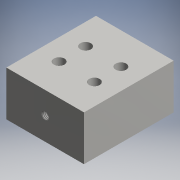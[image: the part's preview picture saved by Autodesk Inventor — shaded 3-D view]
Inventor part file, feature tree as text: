
AUTODESK INVENTOR PART (.ipt)
format: ipt  version: 2016 (Build 200138000, 138)  size: 129,536 bytes
history: native  units: mm (DEFAULTED — no unit token found)
features: sketch x4, extrude x2, hole x2
ambient origin geometry x8: Origin, YZ Plane, XZ Plane, XY Plane, X Axis, Y Axis, Z Axis, Center Point
bodies: Solid1 (feature_tree)
feature tree (8):
  extrude  "Extrusion1"  Depth=44.0mm
  hole  "Hole1"  [1 undecoded]
  extrude  "Extrusion2"  Depth=5.0mm
  sketch  "Sketch2"  dims[d0=50.8mm d1=44.0mm]
  sketch  "Sketch3"  dims[d2=25.4mm d3=0.0mm]
  hole  "Hole2"  [1 undecoded]
  sketch  "Sketch5"  dims[d11=6.0mm d12=6.0mm d13=6.0mm d14=6.0mm d15=20.0mm d16=15.0mm d18=0.0mm d19=5.0mm d20=6.0mm d21=20.594885mm d22=90.0deg d23=2.0mm d24=4.0mm d25=8.0mm d26=3.5mm d27=1.0mm d28=1.0mm]
  sketch  "Sketch4"  dims[d4=4.134mm d5=10.0mm d6=4.0mm d7=2.0mm d8=90.0deg d9=19.05mm d10=20.594885mm]
note: 2 required parameter values undecoded (feature->parameter linkage not recoverable at this tier; creation-order binding heuristic only, values carry confidence <= 0.55)
